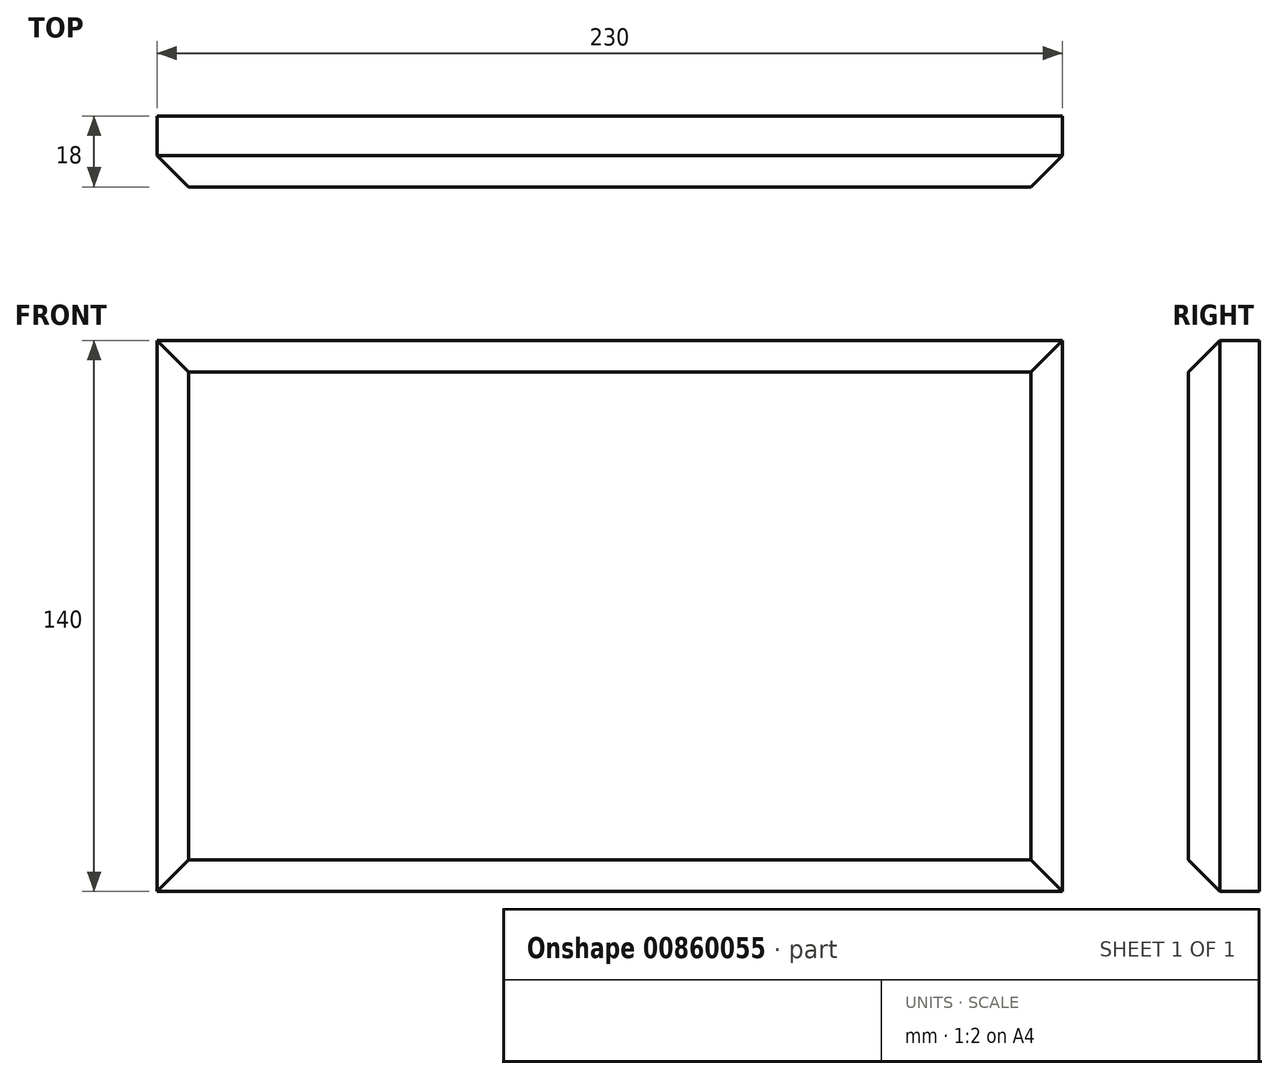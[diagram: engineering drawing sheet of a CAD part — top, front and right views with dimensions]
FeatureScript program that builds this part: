
annotation { "Feature Type Name" : "Feature", "Feature Type Description" : "" }
export const myFeature = defineFeature(function(context is Context, id is Id, definition is map)
    precondition{}
    {
        {
            var Q0;
            Q0=qCreatedBy(makeId("Front.planeOp"),FACE);
            var sketch = newSketch(context, id + "F0", { "sketchPlane" : qUnion([Q0])});
            skLineSegment(sketch, "E0.bottom", {"start": v(-115, 70) * mm, "end": v(115, 70) * mm});
            skLineSegment(sketch, "E0.top", {"start": v(-115, -70) * mm, "end": v(115, -70) * mm});
            skLineSegment(sketch, "E0.left", {"start": v(-115, 70) * mm, "end": v(-115, -70) * mm});
            skLineSegment(sketch, "E0.right", {"start": v(115, 70) * mm, "end": v(115, -70) * mm});
            skPoint(sketch, "E0.middle", {"position": v(0, 0) * mm});
            skSolve(sketch);
        }
        {
            var Q0;
            Q0 = qSketchRegion(id + "F0", true);
            extrude(context, id + "F1", {"entities" : qUnion([Q0]), "depth" : 18 * mm, "offsetDistance" : 25 * mm});
        }
        {
            var Q0;
            Q0=makeQuery(id+"F1.opExtrude","CAP_FACE",FACE,{"disambiguationData":[OSD([sQuery(id+"F0.wireOp",EDGE,"E0.bottom"),sQuery(id+"F0.wireOp",EDGE,"E0.top"),sQuery(id+"F0.wireOp",EDGE,"E0.left"),sQuery(id+"F0.wireOp",EDGE,"E0.right")])],"isStart":false});
            chamfer(context, id + "F2", {"entities" : qUnion([Q0]), "width" : 8 * mm, "tangentPropagation" : true});
        }
    });
